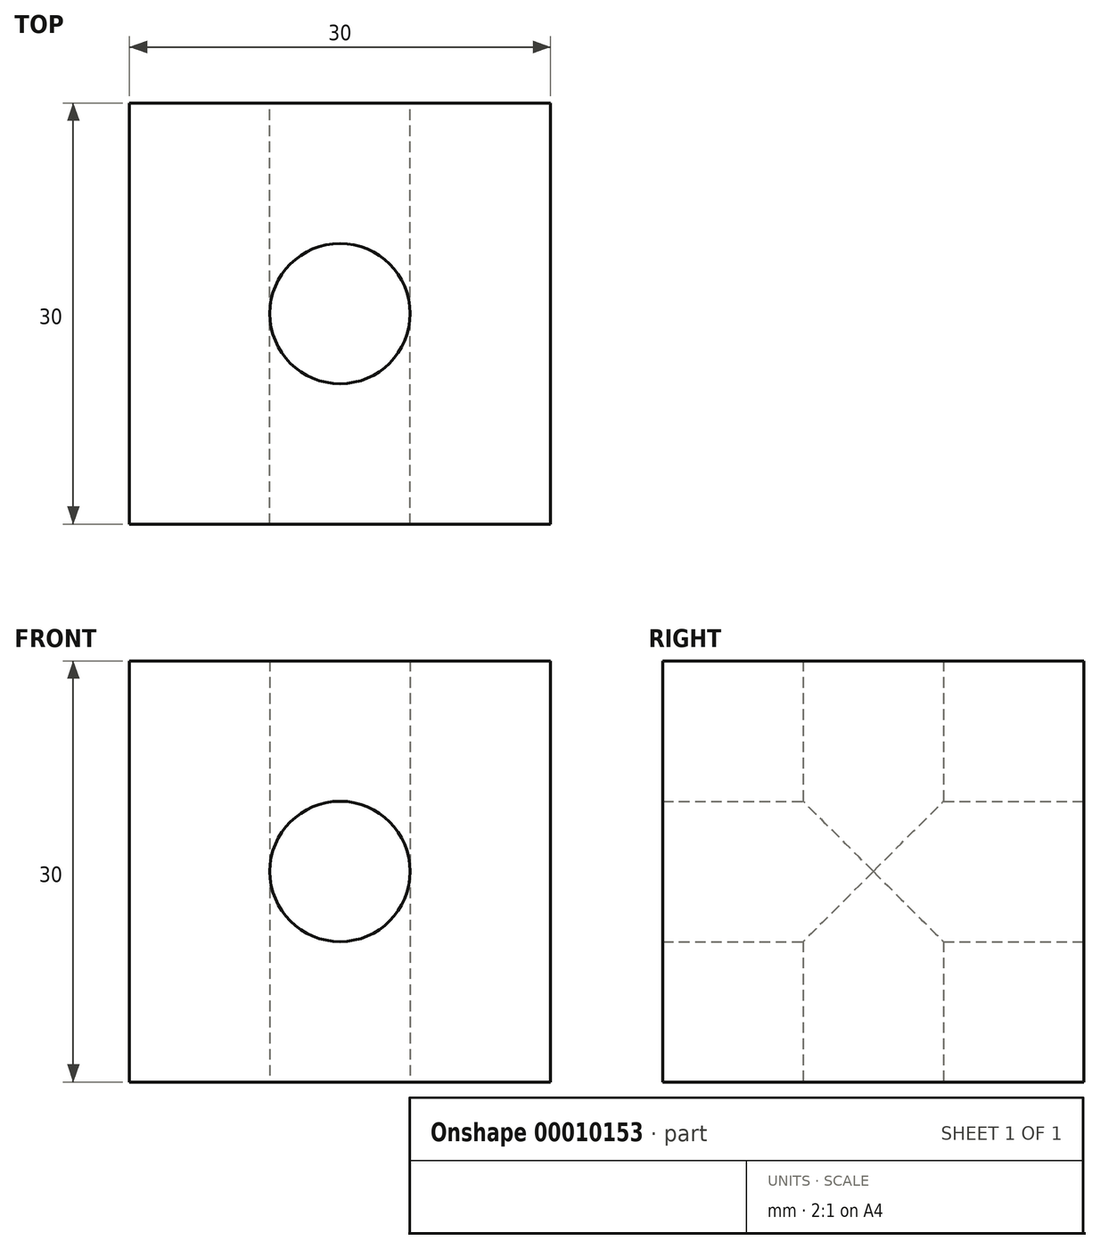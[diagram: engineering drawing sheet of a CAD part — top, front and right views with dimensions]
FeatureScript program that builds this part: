
annotation { "Feature Type Name" : "Feature", "Feature Type Description" : "" }
export const myFeature = defineFeature(function(context is Context, id is Id, definition is map)
    precondition{}
    {
        {
            var Q0;
            Q0=qCreatedBy(makeId("Top.planeOp"),FACE);
            var sketch = newSketch(context, id + "F0", { "sketchPlane" : qUnion([Q0])});
            skLineSegment(sketch, "E0.bottom", {"start": v(0, 0) * mm, "end": v(30, 0) * mm});
            skLineSegment(sketch, "E0.top", {"start": v(0, 30) * mm, "end": v(30, 30) * mm});
            skLineSegment(sketch, "E0.left", {"start": v(0, 0) * mm, "end": v(0, 30) * mm});
            skLineSegment(sketch, "E0.right", {"start": v(30, 0) * mm, "end": v(30, 30) * mm});
            skCircle(sketch, "E1", {"center": v(15, 15) * mm, "radius": 5 * mm});
            skSolve(sketch);
        }
        {
            var Q0;
            Q0=makeQuery(id+"F0.imprint","IMPRINT",FACE,{"disambiguationData":[TD([[makeQuery(id+"F0.imprint","IMPRINT",EDGE,{"derivedFrom":sQuery(id+"F0.wireOp",EDGE,"E0.bottom")}),1.0]])]});
            extrude(context, id + "F1", {"entities" : qUnion([Q0]), "depth" : 30 * mm});
        }
        {
            var Q0;
            Q0=makeQuery(id+"F1.opExtrude","SWEPT_FACE",FACE,{"disambiguationData":[OSD([sQuery(id+"F0.wireOp",EDGE,"E0.top")])]});
            var sketch = newSketch(context, id + "F2", { "sketchPlane" : qUnion([Q0])});
            skCircle(sketch, "E2", {"center": v(-15, 15) * mm, "radius": 5 * mm});
            skSolve(sketch);
        }
        {
            var Q0;
            Q0=makeQuery(id+"F2.imprint","IMPRINT",FACE,{"disambiguationData":[TD([[makeQuery(id+"F2.imprint","IMPRINT",EDGE,{"derivedFrom":sQuery(id+"F2.wireOp",EDGE,"E2")}),1.0]])]});
            extrude(context, id + "F3", {"entities" : qUnion([Q0]), "operationType" : NewBodyOperationType.REMOVE, "endBound" : BoundingType.THROUGH_ALL, "oppositeDirection" : true, "depth" : 25.4 * mm});
        }
    });
